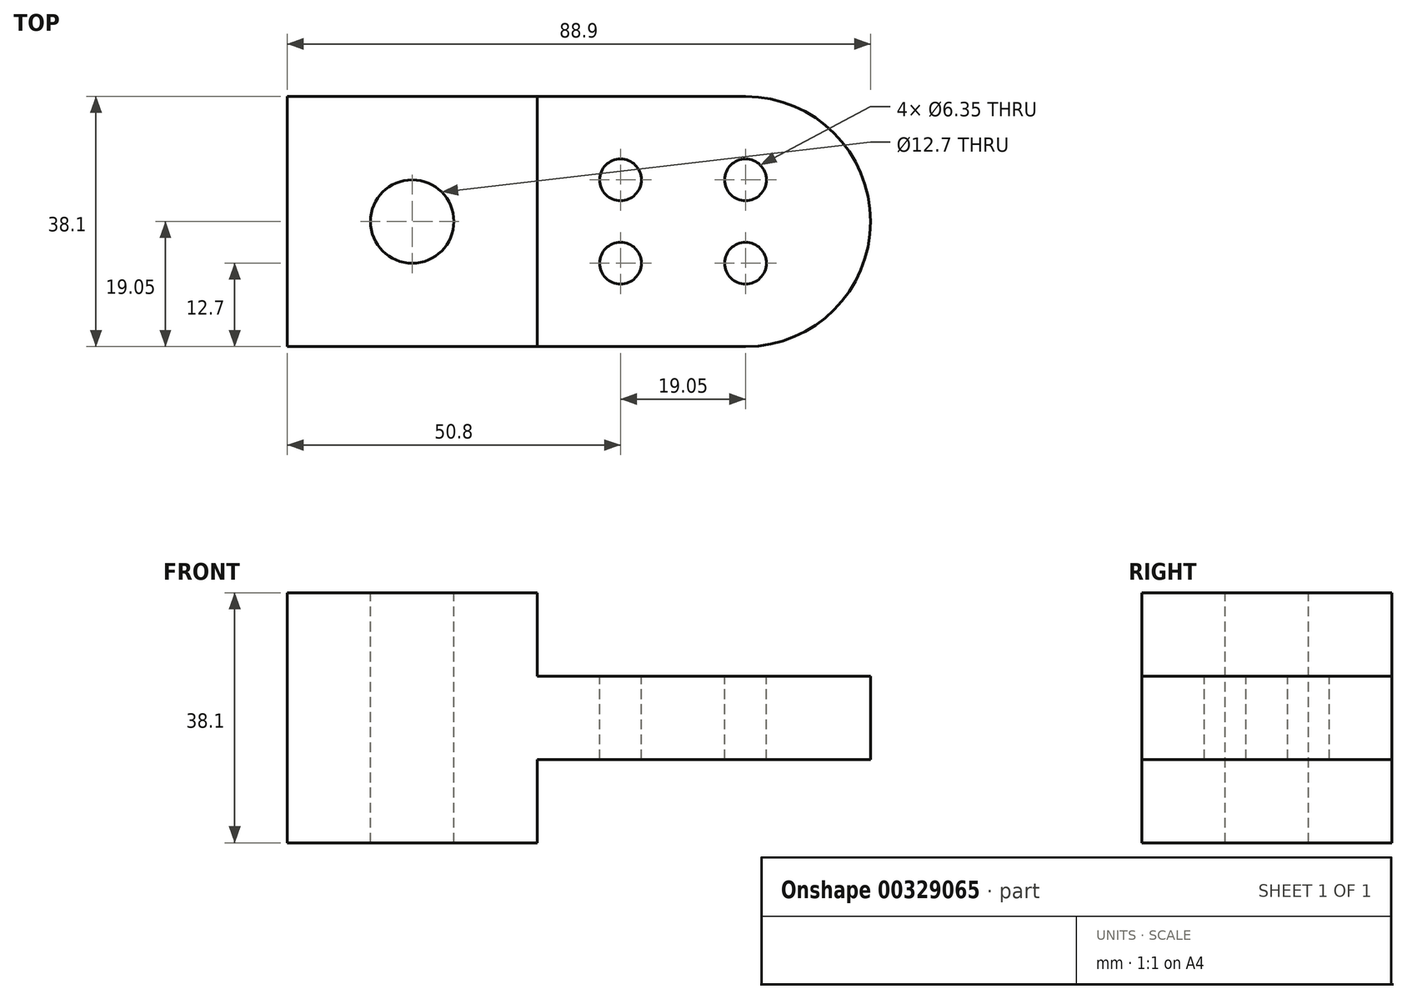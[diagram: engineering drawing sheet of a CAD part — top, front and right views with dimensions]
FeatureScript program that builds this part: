
annotation { "Feature Type Name" : "Feature", "Feature Type Description" : "" }
export const myFeature = defineFeature(function(context is Context, id is Id, definition is map)
    precondition{}
    {
        {
            var Q0;
            Q0=qCreatedBy(makeId("Top.planeOp"),FACE);
            var sketch = newSketch(context, id + "F0", { "sketchPlane" : qUnion([Q0])});
            skLineSegment(sketch, "E0.bottom", {"start": v(0, 0) * mm, "end": v(69.85, 0) * mm});
            skLineSegment(sketch, "E0.top", {"start": v(0, 38.1) * mm, "end": v(69.85, 38.1) * mm});
            skLineSegment(sketch, "E0.left", {"start": v(0, 0) * mm, "end": v(0, 38.1) * mm});
            skArc(sketch, "E1", {"start": v(69.85, 0) * mm, "mid": v(88.9, 19.05) * mm, "end": v(69.85, 38.1) * mm});
            skSolve(sketch);
        }
        {
            var Q0;
            Q0 = qSketchRegion(id + "F0", true);
            extrude(context, id + "F1", {"entities" : qUnion([Q0]), "depth" : 38.1 * mm});
        }
        {
            var Q0;
            Q0=makeQuery(id+"F1.opExtrude","SWEPT_FACE",FACE,{"disambiguationData":[OSD([sQuery(id+"F0.wireOp",EDGE,"E0.bottom")])]});
            var sketch = newSketch(context, id + "F2", { "sketchPlane" : qUnion([Q0])});
            skLineSegment(sketch, "E2.bottom", {"start": v(38.1, 38.1) * mm, "end": v(88.9, 38.1) * mm});
            skLineSegment(sketch, "E2.top", {"start": v(38.1, 25.4) * mm, "end": v(88.9, 25.4) * mm});
            skLineSegment(sketch, "E2.left", {"start": v(38.1, 38.1) * mm, "end": v(38.1, 25.4) * mm});
            skLineSegment(sketch, "E2.right", {"start": v(88.9, 38.1) * mm, "end": v(88.9, 25.4) * mm});
            skSolve(sketch);
        }
        {
            var Q0;
            Q0 = qSketchRegion(id + "F2", true);
            extrude(context, id + "F3", {"entities" : qUnion([Q0]), "operationType" : NewBodyOperationType.REMOVE, "endBound" : BoundingType.THROUGH_ALL, "oppositeDirection" : true, "depth" : 25.4 * mm});
        }
        {
            var Q0;
            Q0=makeQuery(id+"F1.opExtrude","SWEPT_FACE",FACE,{"disambiguationData":[OSD([sQuery(id+"F0.wireOp",EDGE,"E0.bottom")])]});
            var sketch = newSketch(context, id + "F4", { "sketchPlane" : qUnion([Q0])});
            skLineSegment(sketch, "E3.bottom", {"start": v(38.1, 0) * mm, "end": v(88.9, 0) * mm});
            skLineSegment(sketch, "E3.top", {"start": v(38.1, 12.7) * mm, "end": v(88.9, 12.7) * mm});
            skLineSegment(sketch, "E3.left", {"start": v(38.1, 0) * mm, "end": v(38.1, 12.7) * mm});
            skLineSegment(sketch, "E3.right", {"start": v(88.9, 0) * mm, "end": v(88.9, 12.7) * mm});
            skSolve(sketch);
        }
        {
            var Q0;
            Q0 = qSketchRegion(id + "F4", true);
            extrude(context, id + "F5", {"entities" : qUnion([Q0]), "operationType" : NewBodyOperationType.REMOVE, "endBound" : BoundingType.THROUGH_ALL, "oppositeDirection" : true, "depth" : 25.4 * mm});
        }
        {
            var Q0;
            Q0=makeQuery(id+"F1.opExtrude","CAP_FACE",FACE,{"disambiguationData":[OSD([sQuery(id+"F0.wireOp",EDGE,"E0.bottom"),sQuery(id+"F0.wireOp",EDGE,"E0.top"),sQuery(id+"F0.wireOp",EDGE,"E0.left"),sQuery(id+"F0.wireOp",EDGE,"E1")])],"isStart":false});
            var sketch = newSketch(context, id + "F6", { "sketchPlane" : qUnion([Q0])});
            skCircle(sketch, "E4", {"center": v(19.05, 19.05) * mm, "radius": 6.35 * mm});
            skSolve(sketch);
        }
        {
            var Q0;
            Q0 = qSketchRegion(id + "F6", true);
            extrude(context, id + "F7", {"entities" : qUnion([Q0]), "operationType" : NewBodyOperationType.REMOVE, "endBound" : BoundingType.THROUGH_ALL, "oppositeDirection" : true, "depth" : 25.4 * mm});
        }
        {
            var Q0;
            Q0=makeQuery(id+"F3.boolean.opBoolean","COPY",FACE,{"derivedFrom":makeQuery(id+"F3.opExtrude","SWEPT_FACE",FACE,{"disambiguationData":[OSD([sQuery(id+"F2.wireOp",EDGE,"E2.top")])]})});
            var sketch = newSketch(context, id + "F8", { "sketchPlane" : qUnion([Q0])});
            skCircle(sketch, "E5", {"center": v(50.8, 25.4) * mm, "radius": 3.18 * mm});
            skCircle(sketch, "E6", {"center": v(69.85, 25.4) * mm, "radius": 3.18 * mm});
            skCircle(sketch, "E7", {"center": v(50.8, 12.7) * mm, "radius": 3.18 * mm});
            skCircle(sketch, "E8", {"center": v(69.85, 12.7) * mm, "radius": 3.18 * mm});
            skSolve(sketch);
        }
        {
            var Q0;
            Q0 = qSketchRegion(id + "F8", true);
            extrude(context, id + "F9", {"entities" : qUnion([Q0]), "operationType" : NewBodyOperationType.REMOVE, "endBound" : BoundingType.THROUGH_ALL, "oppositeDirection" : true, "depth" : 25.4 * mm});
        }
    });
